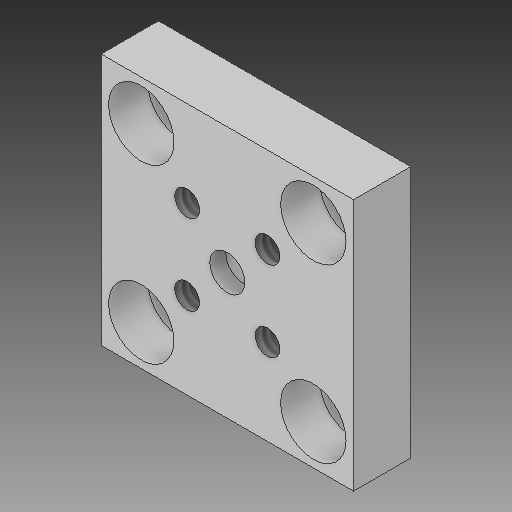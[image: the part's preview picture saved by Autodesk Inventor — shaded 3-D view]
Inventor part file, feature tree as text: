
AUTODESK INVENTOR PART (.ipt)
format: ipt  version: 2019 (Build 230136000, 136)  size: 190,464 bytes
history: native  units: mm
features: sketch x5, hole x4, extrude x1
ambient origin geometry x8: Origin, YZ Plane, XZ Plane, XY Plane, X Axis, Y Axis, Z Axis, Center Point
bodies: Solid1 (feature_tree)
feature tree (10):
  extrude  "Extrusion1"  Depth=22.0mm
  hole  "Hole1"  [1 undecoded]
  hole  "Hole2"  [1 undecoded]
  hole  "Hole5"  [1 undecoded]
  hole  "Hole6"  [1 undecoded]
  sketch  "Sketch1"  dims[d0=22.0mm d1=22.0mm]
  sketch  "Sketch2"  dims[d2=5.0mm d3=0.0mm d4=3.0mm]
  sketch  "Sketch3"  dims[d5=3.0mm d6=3.5mm]
  sketch  "Sketch7"  dims[d7=15.0mm d8=3.5mm]
  sketch  "Sketch8"  dims[d9=3.5mm d10=3.0mm d11=3.5mm d12=3.5mm d13=3.0mm d14=3.5mm d15=3.5mm d16=3.2mm d17=6.0mm d18=5.7mm d19=3.4mm d20=90.0deg d21=0.5mm d22=20.594885mm d23=3.0mm d24=7.5mm d25=7.5mm d26=2.156mm d27=5.69mm d28=5.5mm d29=4.0mm d30=90.0deg d31=8.865mm d32=20.594885mm d33=3.0mm d34=3.0mm d35=3.0mm d36=7.0mm d37=7.0mm d38=7.0mm d39=0.0mm d40=7.5mm d41=7.0mm d64=3.0mm d65=11.0mm d66=11.0mm d67=3.05mm d68=5.69mm d69=4.9mm d70=2.0mm d71=90.0deg d72=8.865mm d73=20.594885mm d74=4.9mm d75=4.9mm d76=8.331mm d77=4.0mm d78=2.0mm d79=90.0deg d80=3.05mm d81=20.594885mm]
note: 4 required parameter values undecoded (feature->parameter linkage not recoverable at this tier; creation-order binding heuristic only, values carry confidence <= 0.55)
